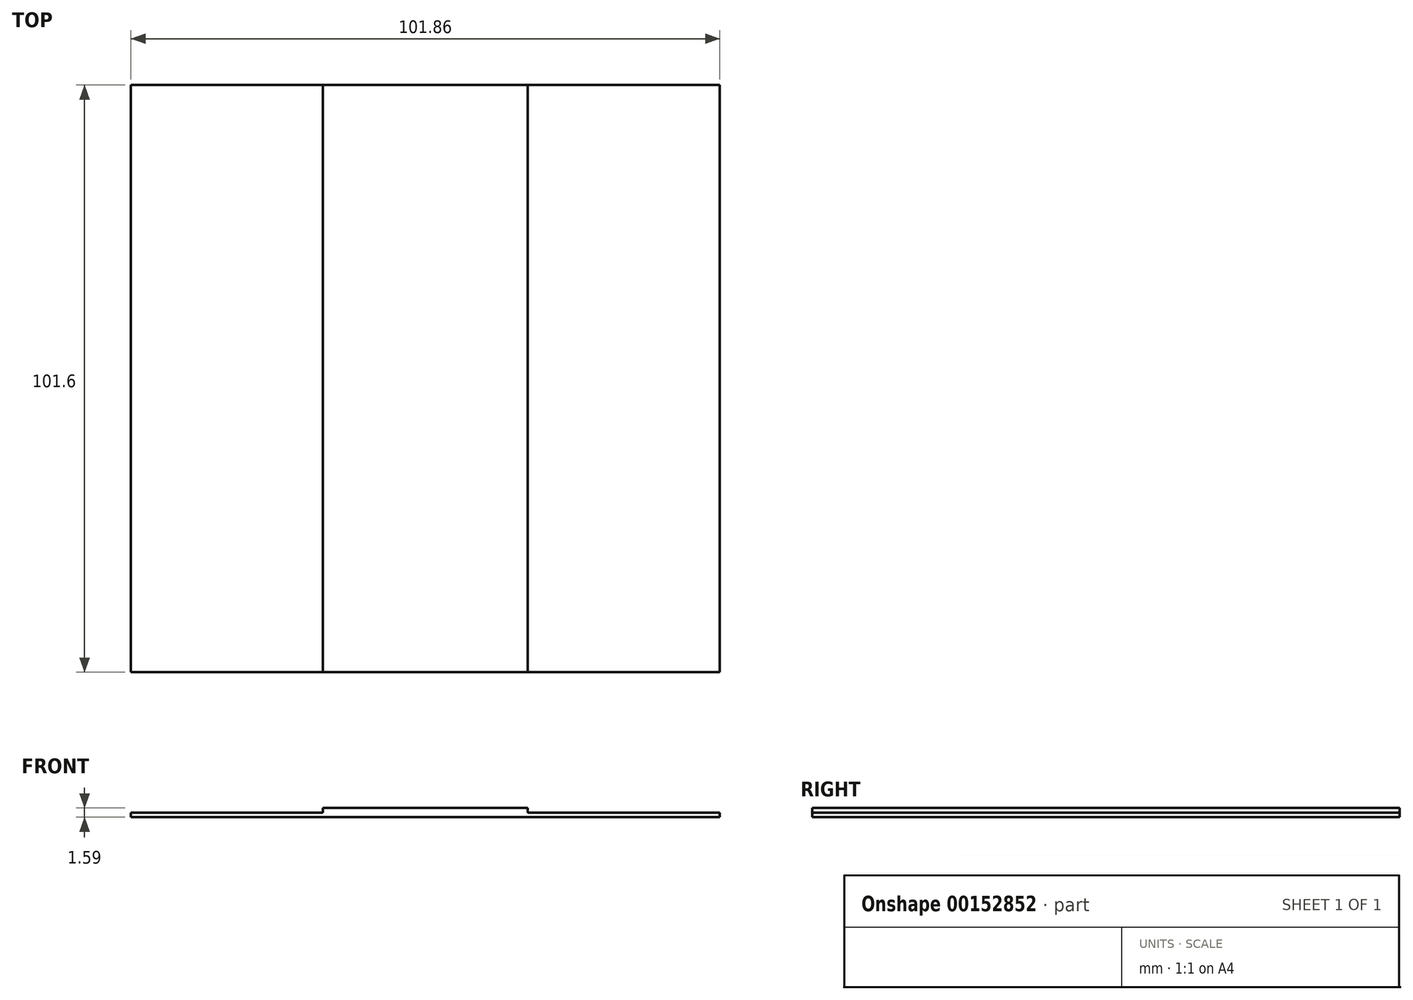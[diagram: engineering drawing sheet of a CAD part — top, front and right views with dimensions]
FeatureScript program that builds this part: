
annotation { "Feature Type Name" : "Feature", "Feature Type Description" : "" }
export const myFeature = defineFeature(function(context is Context, id is Id, definition is map)
    precondition{}
    {
        {
            var Q0;
            Q0=qCreatedBy(makeId("Top.planeOp"),FACE);
            var sketch = newSketch(context, id + "F0", { "sketchPlane" : qUnion([Q0])});
            skLineSegment(sketch, "E0.bottom", {"start": v(50.93, -50.8) * mm, "end": v(-50.93, -50.8) * mm});
            skLineSegment(sketch, "E0.top", {"start": v(50.93, 50.8) * mm, "end": v(-50.93, 50.8) * mm});
            skLineSegment(sketch, "E0.left", {"start": v(50.93, -50.8) * mm, "end": v(50.93, 50.8) * mm});
            skLineSegment(sketch, "E0.right", {"start": v(-50.93, -50.8) * mm, "end": v(-50.93, 50.8) * mm});
            skPoint(sketch, "E0.middle", {"position": v(0, 0) * mm});
            skSolve(sketch);
        }
        {
            var Q0;
            Q0=qSketchRegion(id+"F0",true);
            extrude(context, id + "F1", {"entities" : qUnion([Q0]), "depth" : 0.8 * mm});
        }
        {
            var Q0;
            Q0=makeQuery(id+"F1.opExtrude","CAP_FACE",FACE,{"disambiguationData":[OSD([sQuery(id+"F0.wireOp",EDGE,"E0.bottom"),sQuery(id+"F0.wireOp",EDGE,"E0.top"),sQuery(id+"F0.wireOp",EDGE,"E0.left"),sQuery(id+"F0.wireOp",EDGE,"E0.right")])],"isStart":false});
            var sketch = newSketch(context, id + "F2", { "sketchPlane" : qUnion([Q0])});
            skLineSegment(sketch, "E1.bottom", {"start": v(17.72, -50.8) * mm, "end": v(-17.72, -50.8) * mm});
            skLineSegment(sketch, "E1.top", {"start": v(17.72, 50.8) * mm, "end": v(-17.72, 50.8) * mm});
            skLineSegment(sketch, "E1.left", {"start": v(17.72, -50.8) * mm, "end": v(17.72, 50.8) * mm});
            skLineSegment(sketch, "E1.right", {"start": v(-17.72, -50.8) * mm, "end": v(-17.72, 50.8) * mm});
            skPoint(sketch, "E1.middle", {"position": v(0, 0) * mm});
            skSolve(sketch);
        }
        {
            var Q0;
            Q0=qSketchRegion(id+"F2",true);
            extrude(context, id + "F3", {"entities" : qUnion([Q0]), "operationType" : NewBodyOperationType.ADD, "depth" : 0.8 * mm});
        }
    });
